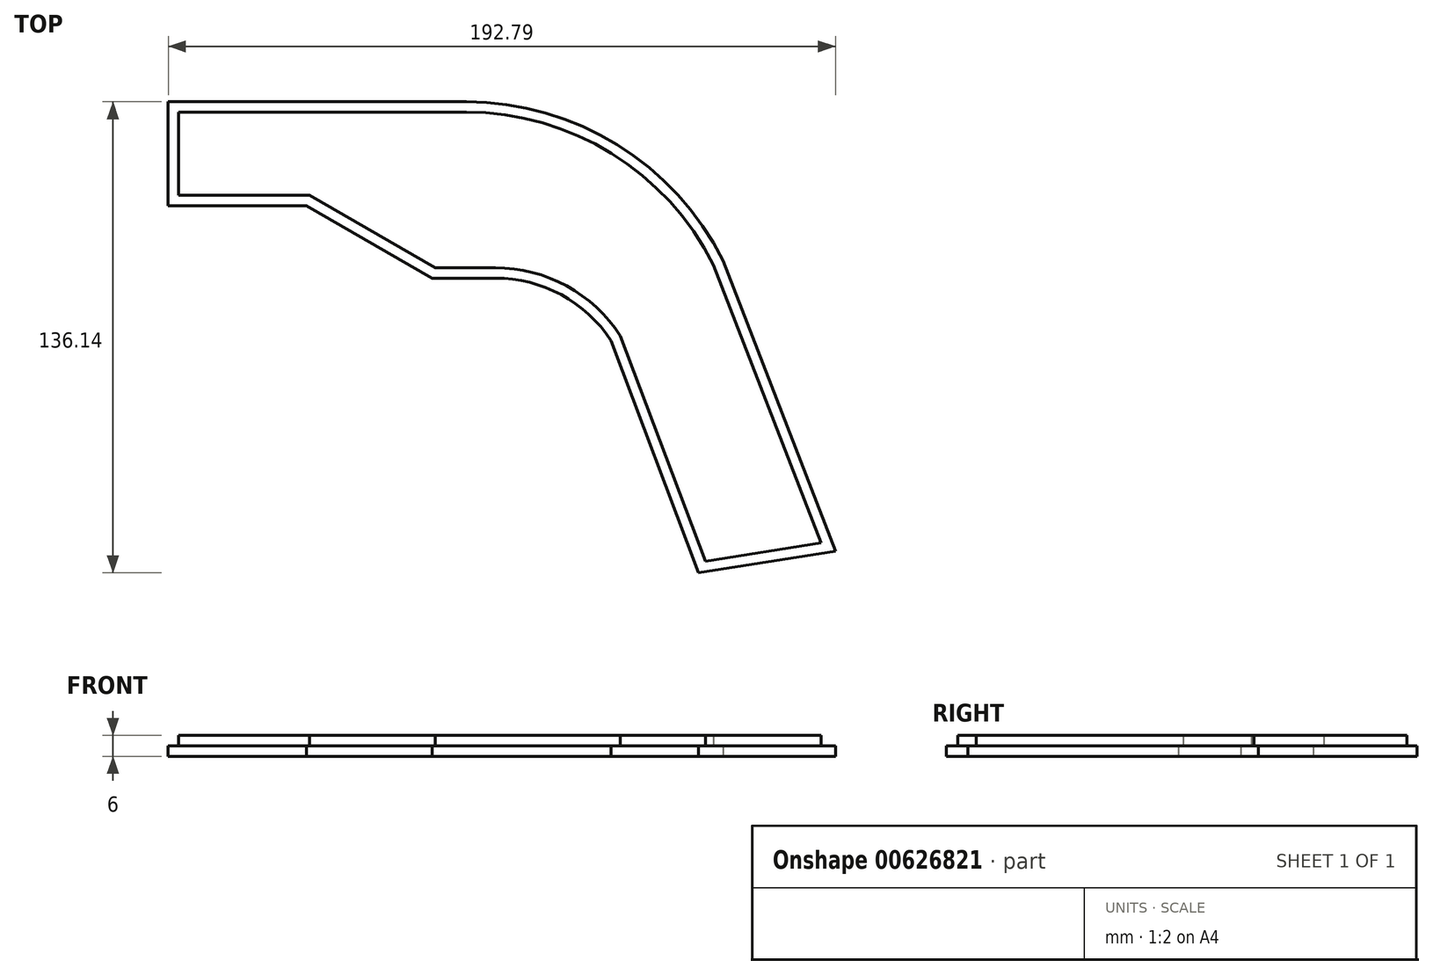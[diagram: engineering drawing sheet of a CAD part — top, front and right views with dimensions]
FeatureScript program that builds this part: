
annotation { "Feature Type Name" : "Feature", "Feature Type Description" : "" }
export const myFeature = defineFeature(function(context is Context, id is Id, definition is map)
    precondition{}
    {
        {
            var Q0;
            Q0=qCreatedBy(makeId("Top.planeOp"),FACE);
            var sketch = newSketch(context, id + "F0", { "sketchPlane" : qUnion([Q0])});
            skLineSegment(sketch, "E0", {"start": v(-112.2, 52.93) * mm, "end": v(-26.05, 52.93) * mm});
            skLineSegment(sketch, "E1", {"start": v(-112.2, 52.93) * mm, "end": v(-112.2, 22.93) * mm});
            skLineSegment(sketch, "E2", {"start": v(-112.2, 22.93) * mm, "end": v(-72.2, 22.93) * mm});
            skLineSegment(sketch, "E3", {"start": v(-72.2, 22.93) * mm, "end": v(-35.87, 1.96) * mm});
            skLineSegment(sketch, "E4", {"start": v(-35.87, 1.96) * mm, "end": v(-17.65, 1.96) * mm});
            skPoint(sketch, "E5", {"position": v(44.54, 15.18) * mm});
            skPoint(sketch, "E6.visualSharp", {"position": v(2.8, 52.93) * mm});
            skPoint(sketch, "E7.end.orphan", {"position": v(134.54, -66.23) * mm});
            skPoint(sketch, "E8.visualSharp", {"position": v(2.8, 1.96) * mm});
            skArc(sketch, "E9", {"start": v(15.8, -16.1) * mm, "mid": v(1.35, -2.85) * mm, "end": v(-17.65, 1.96) * mm});
            skArc(sketch, "E10", {"start": v(48.12, 6.99) * mm, "mid": v(17.57, 40.51) * mm, "end": v(-26.05, 52.93) * mm});
            skLineSegment(sketch, "E11", {"start": v(48.12, 6.99) * mm, "end": v(80.6, -76.94) * mm});
            skLineSegment(sketch, "E12", {"start": v(80.6, -76.94) * mm, "end": v(41.1, -83.2) * mm});
            skLineSegment(sketch, "E13", {"start": v(41.1, -83.2) * mm, "end": v(15.8, -16.1) * mm});
            skSolve(sketch);
        }
        {
            var Q0;
            Q0 = qSketchRegion(id + "F0", true);
            extrude(context, id + "F1", {"entities" : qUnion([Q0]), "depth" : 3 * mm, "offsetDistance" : 25 * mm});
        }
        {
            var Q0;
            Q0=makeQuery(id+"F1.opExtrude","CAP_FACE",FACE,{"disambiguationData":[OSD([sQuery(id+"F0.wireOp",EDGE,"E0"),sQuery(id+"F0.wireOp",EDGE,"E1"),sQuery(id+"F0.wireOp",EDGE,"E2"),sQuery(id+"F0.wireOp",EDGE,"E3"),sQuery(id+"F0.wireOp",EDGE,"E4"),sQuery(id+"F0.wireOp",EDGE,"E9"),sQuery(id+"F0.wireOp",EDGE,"E10"),sQuery(id+"F0.wireOp",EDGE,"E11"),sQuery(id+"F0.wireOp",EDGE,"E12"),sQuery(id+"F0.wireOp",EDGE,"E13")])],"isStart":false});
            var sketch = newSketch(context, id + "F2", { "sketchPlane" : qUnion([Q0])});
            skArc(sketch, "E14.0", {"start": v(-17.65, 4.96) * mm, "mid": v(2.92, -0.29) * mm, "end": v(18.48, -14.74) * mm});
            skLineSegment(sketch, "E14.1", {"start": v(-35.06, 4.96) * mm, "end": v(-17.65, 4.96) * mm});
            skLineSegment(sketch, "E14.2", {"start": v(18.48, -14.74) * mm, "end": v(43.04, -79.86) * mm});
            skLineSegment(sketch, "E14.3", {"start": v(-71.39, 25.93) * mm, "end": v(-35.06, 4.96) * mm});
            skLineSegment(sketch, "E14.4", {"start": v(-109.2, 25.93) * mm, "end": v(-71.39, 25.93) * mm});
            skLineSegment(sketch, "E14.5", {"start": v(-109.2, 49.93) * mm, "end": v(-109.2, 25.93) * mm});
            skLineSegment(sketch, "E14.6", {"start": v(43.04, -79.86) * mm, "end": v(76.46, -74.56) * mm});
            skLineSegment(sketch, "E14.7", {"start": v(76.46, -74.56) * mm, "end": v(45.37, 5.78) * mm});
            skArc(sketch, "E14.8", {"start": v(45.37, 5.78) * mm, "mid": v(15.93, 38) * mm, "end": v(-26.05, 49.93) * mm});
            skLineSegment(sketch, "E14.9", {"start": v(-26.05, 49.93) * mm, "end": v(-109.2, 49.93) * mm});
            skSolve(sketch);
        }
        {
            var Q0;
            Q0 = qSketchRegion(id + "F2", true);
            extrude(context, id + "F3", {"entities" : qUnion([Q0]), "operationType" : NewBodyOperationType.ADD, "depth" : 3 * mm, "offsetDistance" : 25 * mm});
        }
    });
